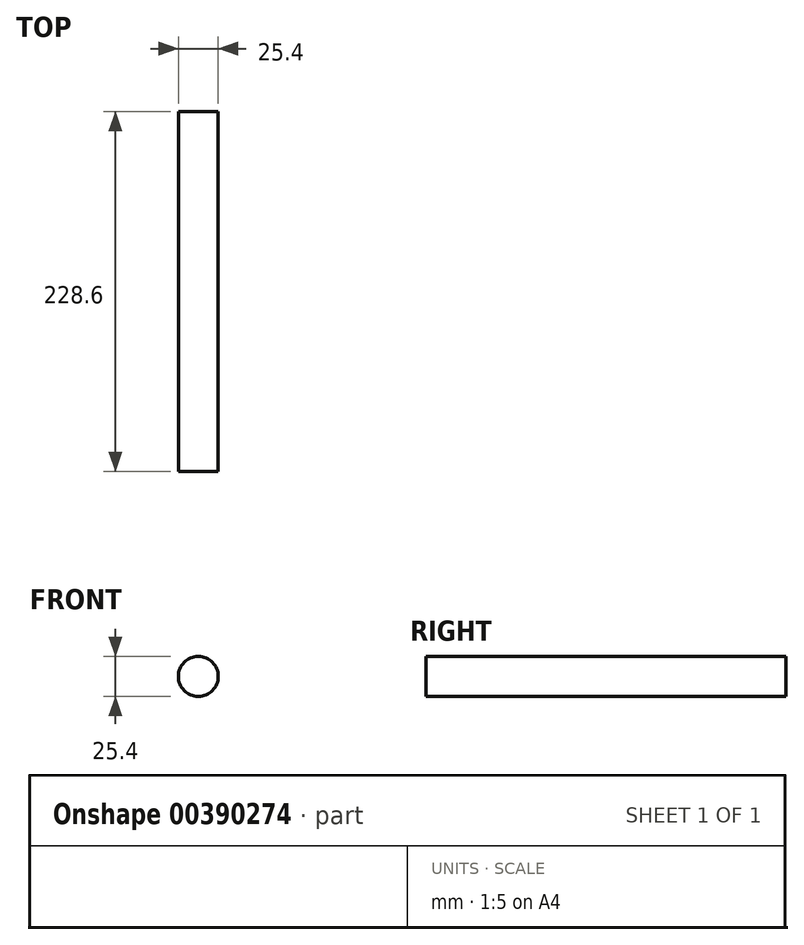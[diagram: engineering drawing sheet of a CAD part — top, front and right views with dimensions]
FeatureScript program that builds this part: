
annotation { "Feature Type Name" : "Feature", "Feature Type Description" : "" }
export const myFeature = defineFeature(function(context is Context, id is Id, definition is map)
    precondition{}
    {
        {
            var Q0;
            Q0=qCreatedBy(makeId("Front.planeOp"),FACE);
            var sketch = newSketch(context, id + "F0", { "sketchPlane" : qUnion([Q0])});
            skCircle(sketch, "E0", {"center": v(0, 0) * mm, "radius": 12.7 * mm});
            skSolve(sketch);
        }
        {
            var Q0;
            Q0 = qSketchRegion(id + "F0", true);
            extrude(context, id + "F1", {"entities" : qUnion([Q0]), "depth" : 228.6 * mm, "offsetDistance" : 25.4 * mm});
        }
    });
